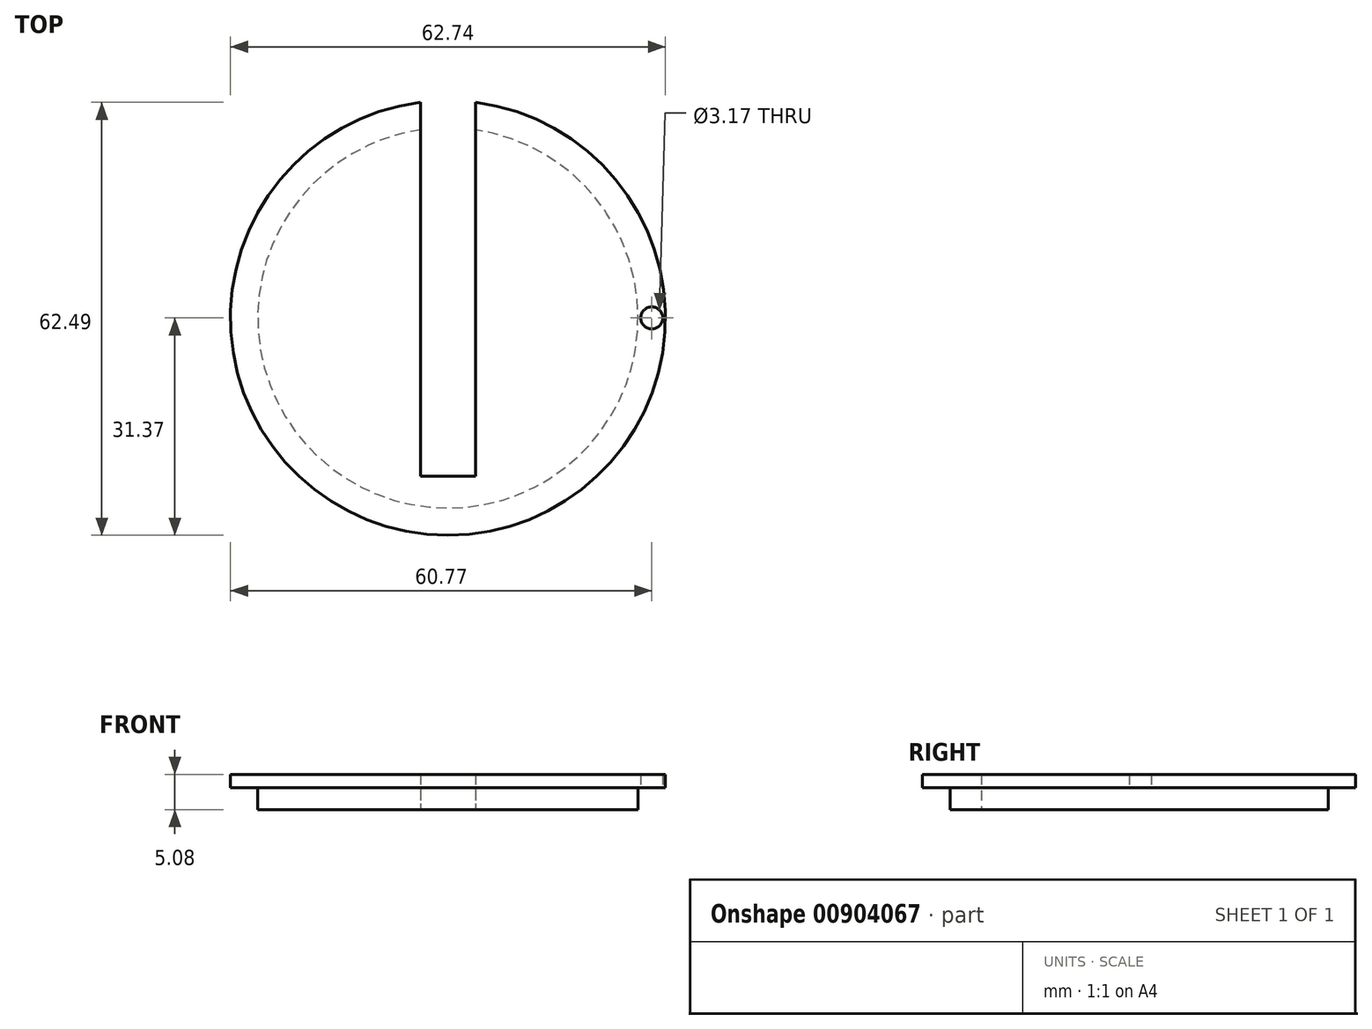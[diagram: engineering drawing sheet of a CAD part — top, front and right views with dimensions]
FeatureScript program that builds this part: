
annotation { "Feature Type Name" : "Feature", "Feature Type Description" : "" }
export const myFeature = defineFeature(function(context is Context, id is Id, definition is map)
    precondition{}
    {
        {
            var Q0;
            Q0=qCreatedBy(makeId("Top.planeOp"),FACE);
            var sketch = newSketch(context, id + "F0", { "sketchPlane" : qUnion([Q0])});
            skArc(sketch, "E0", {"start": v(-3.97, 31.12) * mm, "mid": v(0, -31.37) * mm, "end": v(3.97, 31.12) * mm});
            skLineSegment(sketch, "E1", {"start": v(0, -15.85) * mm, "end": v(0, 31.37) * mm, "construction": true});
            skLineSegment(sketch, "E2", {"start": v(-3.97, 31.12) * mm, "end": v(-3.97, -22.86) * mm});
            skLineSegment(sketch, "E3.MirrorCS", {"start": v(3.97, 31.12) * mm, "end": v(3.97, -22.86) * mm});
            skLineSegment(sketch, "E4", {"start": v(-3.97, -22.86) * mm, "end": v(3.97, -22.86) * mm});
            skSolve(sketch);
        }
        {
            var Q0;
            Q0=makeQuery(id+"F0.imprint","IMPRINT",FACE,{"disambiguationData":[TD([[makeQuery(id+"F0.imprint","IMPRINT",EDGE,{"derivedFrom":sQuery(id+"F0.wireOp",EDGE,"E0")}),1.0]])]});
            extrude(context, id + "F1", {"entities" : qUnion([Q0]), "flatOperationType" : FlatOperationType.REMOVE, "depth" : 5.08 * mm, "offsetDistance" : 25.4 * mm, "domain" : OperationDomain.MODEL});
        }
        {
            var Q0;
            Q0=qCreatedBy(makeId("Top.planeOp"),FACE);
            var sketch = newSketch(context, id + "F2", { "sketchPlane" : qUnion([Q0])});
            skCircle(sketch, "E5", {"center": v(0, 0) * mm, "radius": 27.43 * mm});
            skArc(sketch, "E6.0", {"start": v(-3.97, 31.12) * mm, "mid": v(0, -31.37) * mm, "end": v(3.97, 31.12) * mm});
            skLineSegment(sketch, "E7.0", {"start": v(3.97, 31.12) * mm, "end": v(3.97, -22.86) * mm});
            skLineSegment(sketch, "E8.0", {"start": v(-3.97, 31.12) * mm, "end": v(-3.97, -22.86) * mm});
            skSolve(sketch);
        }
        {
            var Q0;
            {var subQ5=sQuery(id+"F2.wireOp",EDGE,"E6.0");Q0=makeQuery(id+"F2.imprint","IMPRINT",FACE,{"disambiguationData":[TD([[makeQuery(id+"F2.imprint","IMPRINT",EDGE,{"derivedFrom":subQ5}),1.0]])]});}
            extrude(context, id + "F3", {"entities" : qUnion([Q0]), "operationType" : NewBodyOperationType.REMOVE, "depth" : 3.17 * mm, "offsetDistance" : 25.4 * mm});
        }
        {
            var Q0;
            Q0=makeQuery(id+"F3.boolean.opBoolean","COPY",FACE,{"derivedFrom":makeQuery(id+"F3.opExtrude","CAP_FACE",FACE,{"disambiguationData":[OSD([sQuery(id+"F2.wireOp",EDGE,"E5"),sQuery(id+"F2.wireOp",EDGE,"E6.0"),sQuery(id+"F2.wireOp",EDGE,"E7.0"),sQuery(id+"F2.wireOp",EDGE,"E8.0")])],"isStart":false})});
            var sketch = newSketch(context, id + "F4", { "sketchPlane" : qUnion([Q0])});
            skLineSegment(sketch, "E9", {"start": v(27.43, 0) * mm, "end": v(31.37, 0) * mm, "construction": true});
            skArc(sketch, "E10.0", {"start": v(-3.97, -27.14) * mm, "mid": v(0, 27.43) * mm, "end": v(3.97, -27.14) * mm, "construction": true});
            skArc(sketch, "E11.0", {"start": v(-3.97, -31.12) * mm, "mid": v(0, 31.37) * mm, "end": v(3.97, -31.12) * mm, "construction": true});
            skCircle(sketch, "E12", {"center": v(29.4, 0) * mm, "radius": 1.59 * mm});
            skSolve(sketch);
        }
        {
            var Q0;
            Q0=makeQuery(id+"F4.imprint","IMPRINT",FACE,{"disambiguationData":[TD([[makeQuery(id+"F4.imprint","IMPRINT",EDGE,{"derivedFrom":sQuery(id+"F4.wireOp",EDGE,"E12")}),1.0]])]});
            extrude(context, id + "F5", {"entities" : qUnion([Q0]), "operationType" : NewBodyOperationType.REMOVE, "oppositeDirection" : true, "depth" : 25.4 * mm, "offsetDistance" : 25.4 * mm});
        }
    });
